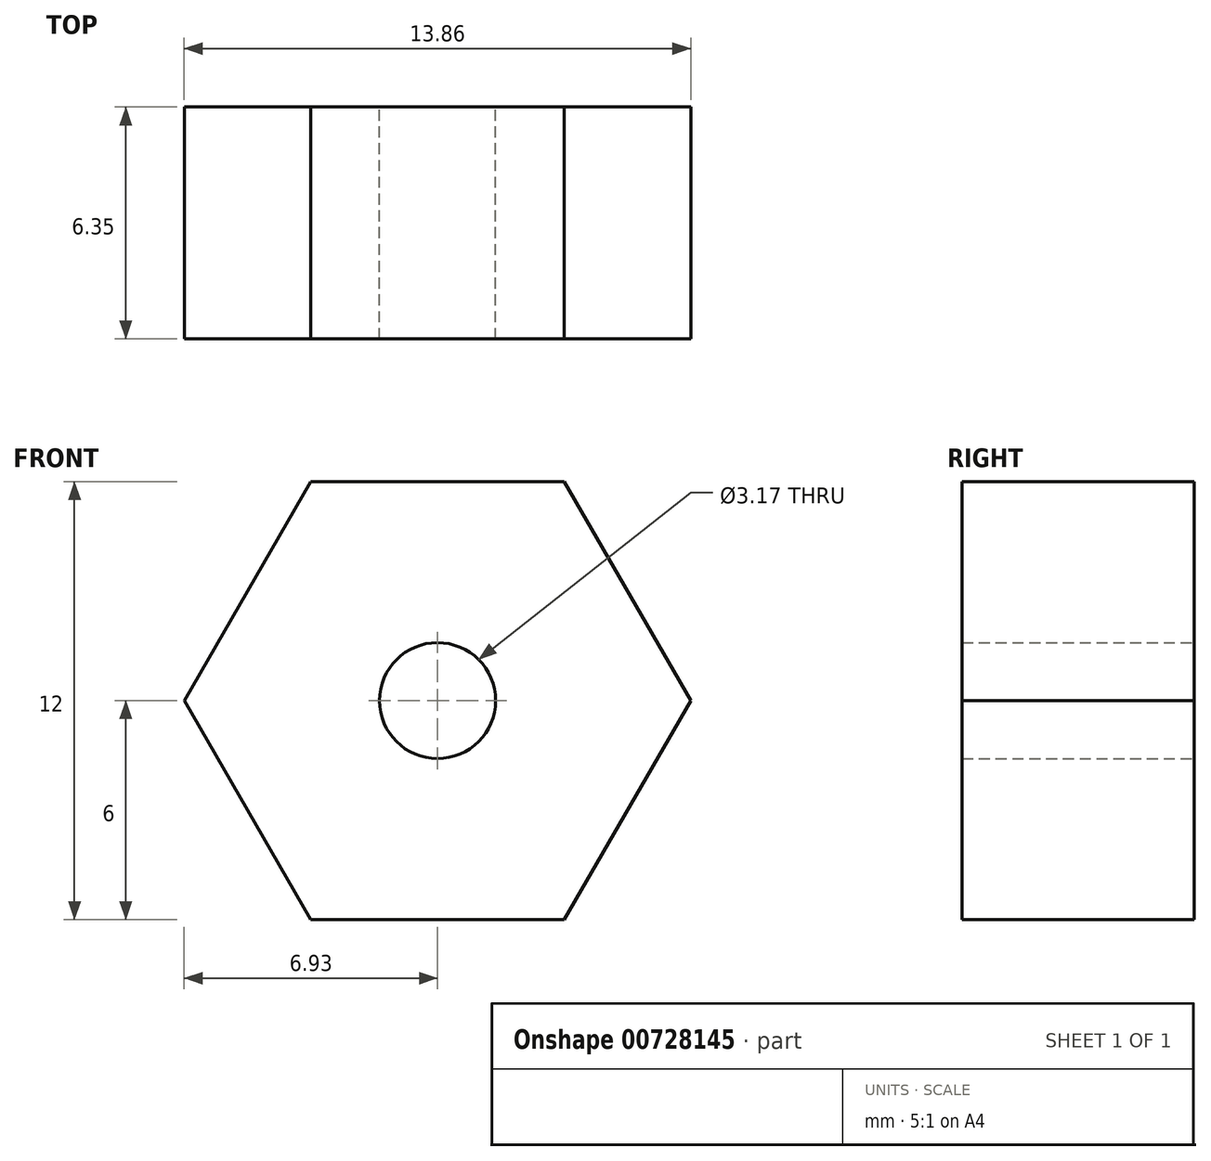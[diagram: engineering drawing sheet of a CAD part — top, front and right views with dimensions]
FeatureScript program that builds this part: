
annotation { "Feature Type Name" : "Feature", "Feature Type Description" : "" }
export const myFeature = defineFeature(function(context is Context, id is Id, definition is map)
    precondition{}
    {
        {
            var Q0;
            Q0=qCreatedBy(makeId("Front.planeOp"),FACE);
            var sketch = newSketch(context, id + "F0", { "sketchPlane" : qUnion([Q0])});
            skCircle(sketch, "E0.cCircle", {"center": v(0, 0) * mm, "radius": 6.93 * mm, "construction": true});
            skLineSegment(sketch, "E0.0", {"start": v(3.46, 6) * mm, "end": v(6.93, 0) * mm});
            skLineSegment(sketch, "E0.1", {"start": v(6.93, 0) * mm, "end": v(3.46, -6) * mm});
            skLineSegment(sketch, "E0.2", {"start": v(3.46, -6) * mm, "end": v(-3.46, -6) * mm});
            skLineSegment(sketch, "E0.3", {"start": v(-3.46, -6) * mm, "end": v(-6.93, 0) * mm});
            skLineSegment(sketch, "E0.4", {"start": v(-6.93, 0) * mm, "end": v(-3.46, 6) * mm});
            skLineSegment(sketch, "E0.5", {"start": v(-3.46, 6) * mm, "end": v(3.46, 6) * mm});
            skCircle(sketch, "E1", {"center": v(0, 0) * mm, "radius": 1.59 * mm});
            skSolve(sketch);
        }
        {
            var Q0;
            Q0=makeQuery(id+"F0.imprint","IMPRINT",FACE,{"disambiguationData":[TD([[makeQuery(id+"F0.imprint","IMPRINT",EDGE,{"derivedFrom":sQuery(id+"F0.wireOp",EDGE,"E0.0")}),-1.0]])]});
            extrude(context, id + "F1", {"entities" : qUnion([Q0]), "depth" : 6.35 * mm, "offsetDistance" : 25.4 * mm});
        }
    });
